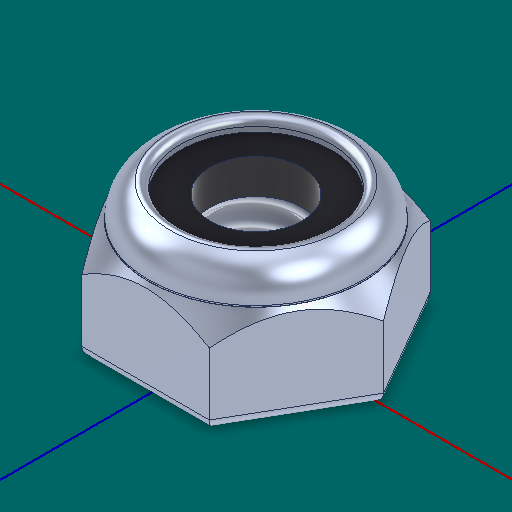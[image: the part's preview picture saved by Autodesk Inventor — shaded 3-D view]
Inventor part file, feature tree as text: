
AUTODESK INVENTOR PART (.ipt)
format: ipt  version: 2025 (Build 290162000, 162)  size: 230,912 bytes
history: native  units: in
note: dims shown in document units (in); Inventor stores cm internally (conversion verified against a paired STEP export)
features: other x4, sketch x2, plane x1
ambient origin geometry x8: Origin, YZ Plane, XZ Plane, XY Plane, X Axis, Y Axis, Z Axis, Center Point
bodies: Body1 (feature_tree)
feature tree (7):
  other  "Nut Thin Nylock.ipt"
  other  "NONE::Nut Thin Nylock.ipt"
  other  "TaggingFeature1"
  sketch  "Sketch1"  dims[d0=0.3937in]
  sketch  "Sketch2"
  plane  "Work Plane1"
  parser-record x1  (decoder bookkeeping rows leaked as tree rows — omitted from the tree; the rows remain in map.json)
